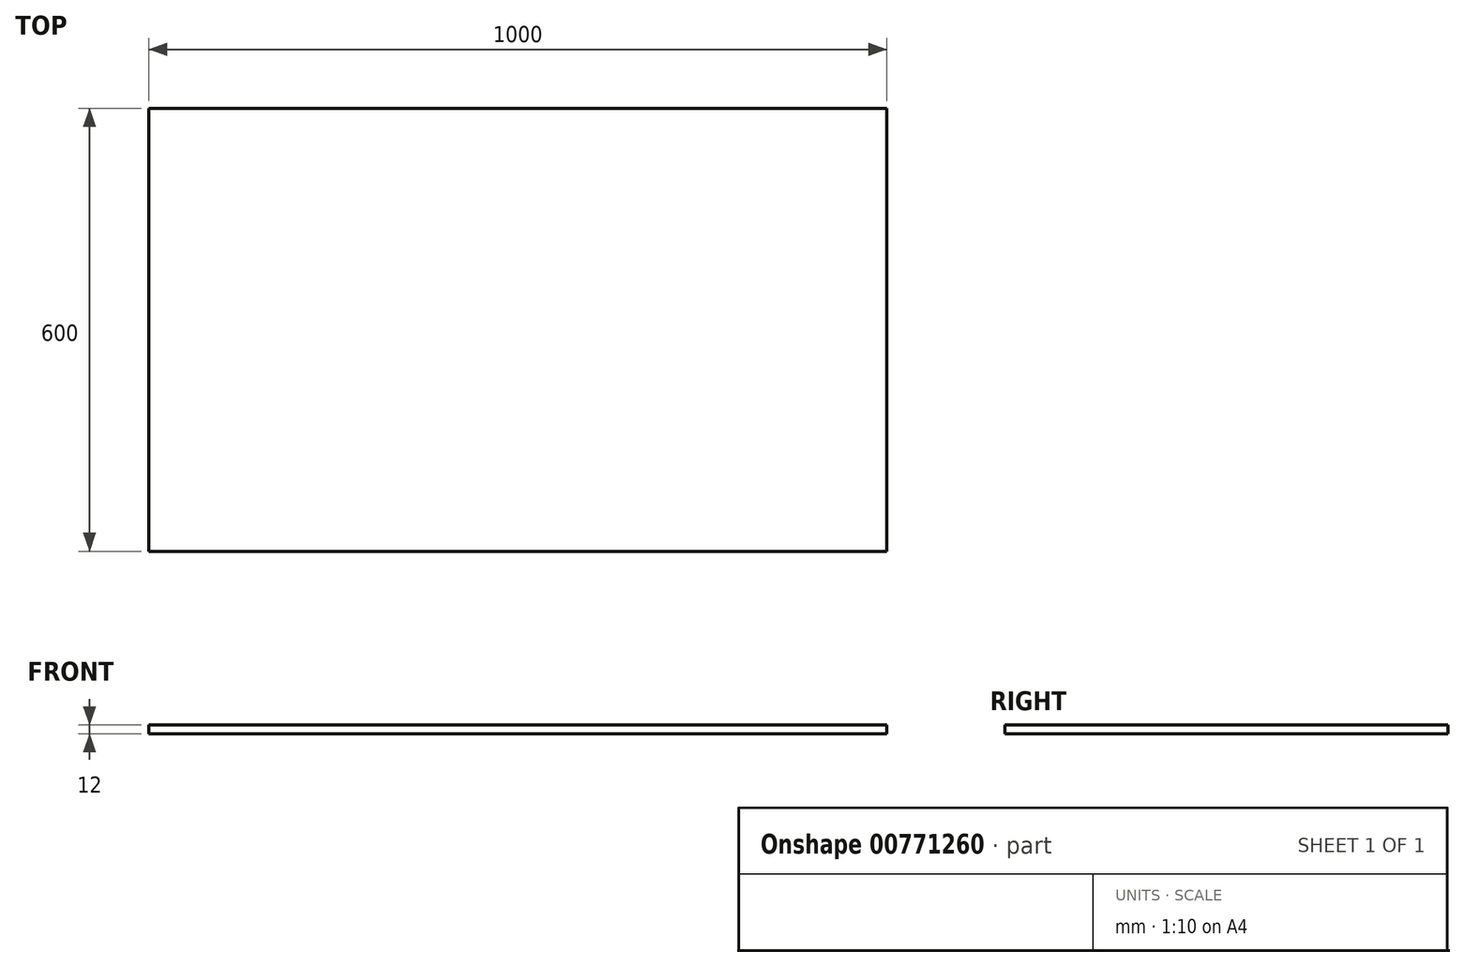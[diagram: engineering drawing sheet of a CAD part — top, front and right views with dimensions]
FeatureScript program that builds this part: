
annotation { "Feature Type Name" : "Feature", "Feature Type Description" : "" }
export const myFeature = defineFeature(function(context is Context, id is Id, definition is map)
    precondition{}
    {
        {
            var Q0;
            Q0=qCreatedBy(makeId("Top.planeOp"),FACE);
            var sketch = newSketch(context, id + "F0", { "sketchPlane" : qUnion([Q0])});
            skLineSegment(sketch, "E0.bottom", {"start": v(-500, 300) * mm, "end": v(500, 300) * mm});
            skLineSegment(sketch, "E0.top", {"start": v(-500, -300) * mm, "end": v(500, -300) * mm});
            skLineSegment(sketch, "E0.left", {"start": v(-500, 300) * mm, "end": v(-500, -300) * mm});
            skLineSegment(sketch, "E0.right", {"start": v(500, 300) * mm, "end": v(500, -300) * mm});
            skPoint(sketch, "E0.middle", {"position": v(0, 0) * mm});
            skSolve(sketch);
        }
        {
            var Q0;
            Q0 = qSketchRegion(id + "F0", true);
            extrude(context, id + "F1", {"entities" : qUnion([Q0]), "depth" : 12 * mm, "offsetDistance" : 25 * mm});
        }
    });
